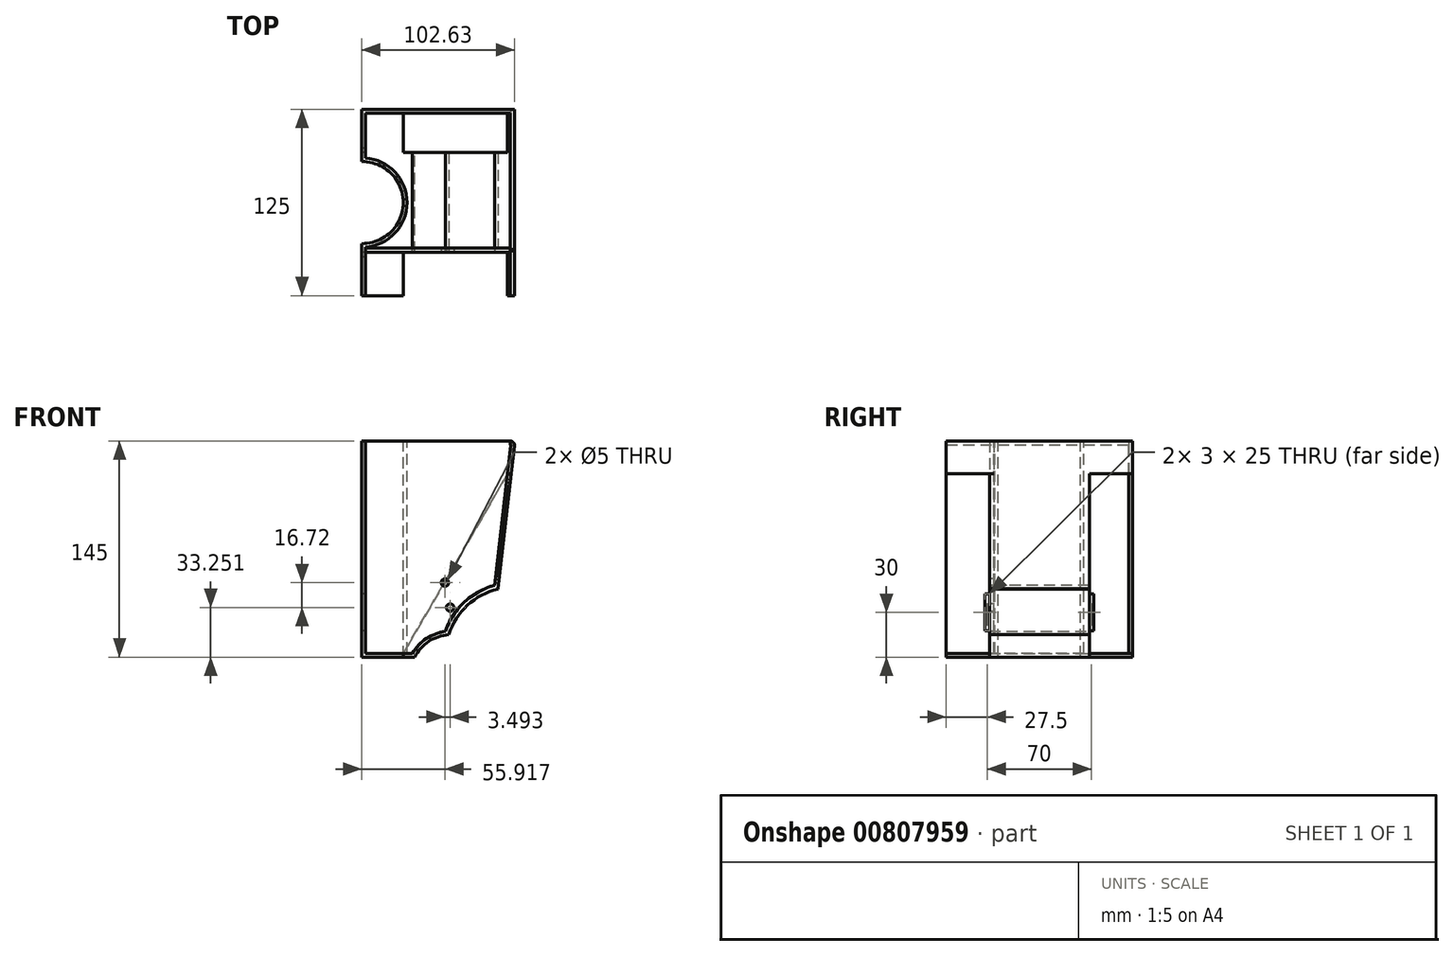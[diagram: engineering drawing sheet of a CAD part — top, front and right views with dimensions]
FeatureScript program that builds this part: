
annotation { "Feature Type Name" : "Feature", "Feature Type Description" : "" }
export const myFeature = defineFeature(function(context is Context, id is Id, definition is map)
    precondition{}
    {
        {
            var Q0;
            Q0=qCreatedBy(makeId("Front.planeOp"),FACE);
            var sketch = newSketch(context, id + "F0", { "sketchPlane" : qUnion([Q0])});
            skLineSegment(sketch, "E0", {"start": v(0, 130) * mm, "end": v(75, 130) * mm});
            skArc(sketch, "E1", {"start": v(56.58, -15) * mm, "mid": v(32.08, 0) * mm, "end": v(7.59, -15) * mm});
            skLineSegment(sketch, "E2", {"start": v(0, -15) * mm, "end": v(7.59, -15) * mm});
            skLineSegment(sketch, "E3.trimOffspring", {"start": v(56.58, -15) * mm, "end": v(58.27, -15) * mm});
            skLineSegment(sketch, "E4", {"start": v(75, 130) * mm, "end": v(58.27, -15) * mm});
            skLineSegment(sketch, "E5", {"start": v(0, 130) * mm, "end": v(-28, 130) * mm});
            skLineSegment(sketch, "E6", {"start": v(0, -15) * mm, "end": v(-28, -15) * mm});
            skLineSegment(sketch, "E7", {"start": v(-28, -15) * mm, "end": v(-28, 130) * mm});
            skLineSegment(sketch, "E8", {"start": v(75.45, 0) * mm, "end": v(-49.86, 0) * mm, "construction": true});
            skLineSegment(sketch, "E9", {"start": v(0, -37.66) * mm, "end": v(0, 158.2) * mm, "construction": true});
            skSolve(sketch);
        }
        {
            var Q0;
            Q0=makeQuery(id+"F0.imprint","IMPRINT",FACE,{"disambiguationData":[TD([[makeQuery(id+"F0.imprint","IMPRINT",EDGE,{"derivedFrom":sQuery(id+"F0.wireOp",EDGE,"AEWyvxpA-VYwD-7hNY-brtb-rKHveOHAXlaS")}),-1.0]])]});
            var Q1;
            Q1=makeQuery(id+"F0.imprint","IMPRINT",FACE,{"disambiguationData":[TD([[makeQuery(id+"F0.imprint","IMPRINT",EDGE,{"derivedFrom":sQuery(id+"F0.wireOp",EDGE,"E0")}),-1.0]])]});
            extrude(context, id + "F1", {"entities" : qUnion([Q0, Q1]), "depth" : 125 * mm, "offsetDistance" : 25 * mm});
        }
        {
            var Q0;
            Q0=makeQuery(id+"F1.opExtrude","SWEPT_FACE",FACE,{"disambiguationData":[OSD([sQuery(id+"F0.wireOp",EDGE,"E0"),sQuery(id+"F0.wireOp",EDGE,"E5")])]});
            cPlane(context, id + "F2", {"entities" : qUnion([Q0]), "cplaneType" : CPlaneType.OFFSET, "offset" : 0 * mm, "width" : 150 * mm, "height" : 150 * mm});
        }
        {
            var Q0;
            Q0=qCreatedBy(id+"F2.planeOp",FACE);
            var sketch = newSketch(context, id + "F3", { "sketchPlane" : qUnion([Q0])});
            skCircle(sketch, "E10", {"center": v(-27.5, -62.5) * mm, "radius": 27.5 * mm});
            skLineSegment(sketch, "E11", {"start": v(0, 0) * mm, "end": v(0, -125) * mm, "construction": true});
            skLineSegment(sketch, "E12", {"start": v(0, 0) * mm, "end": v(0, -62.5) * mm, "construction": true});
            skSolve(sketch);
        }
        {
            var Q0;
            Q0=makeQuery(id+"F3.imprint","IMPRINT",FACE,{"disambiguationData":[TD([[makeQuery(id+"F3.imprint","IMPRINT",EDGE,{"derivedFrom":sQuery(id+"F3.wireOp",EDGE,"E10")}),1.0]])]});
            extrude(context, id + "F4", {"entities" : qUnion([Q0]), "operationType" : NewBodyOperationType.REMOVE, "oppositeDirection" : true, "depth" : 171.8 * mm, "offsetDistance" : 25 * mm});
        }
        {
            var Q0;
            Q0=makeQuery(id+"F1.opExtrude","SWEPT_EDGE",EDGE,{"disambiguationData":[OSD([sQuery(id+"F0.wireOp",EDGE,"E0"),sQuery(id+"F0.wireOp",EDGE,"E4")])]});
            fillet(context, id + "F5", {"entities" : qUnion([Q0]), "radius" : 3 * mm, "tangentPropagation" : true, "allowEdgeOverflow" : false});
        }
        {
            var Q0;
            Q0=makeQuery(id+"F1.opExtrude","SWEPT_FACE",FACE,{"disambiguationData":[OSD([sQuery(id+"F0.wireOp",EDGE,"E0"),sQuery(id+"F0.wireOp",EDGE,"E5")])]});
            var Q1;
            Q1=makeQuery(id+"F1.opExtrude","CAP_FACE",FACE,{"disambiguationData":[OSD([sQuery(id+"F0.wireOp",EDGE,"E0"),sQuery(id+"F0.wireOp",EDGE,"E1"),sQuery(id+"F0.wireOp",EDGE,"E2"),sQuery(id+"F0.wireOp",EDGE,"E3.trimOffspring"),sQuery(id+"F0.wireOp",EDGE,"E4"),sQuery(id+"F0.wireOp",EDGE,"E5"),sQuery(id+"F0.wireOp",EDGE,"E6"),sQuery(id+"F0.wireOp",EDGE,"E7")])],"isStart":false});
            shell(context, id + "F6", {"entities" : qUnion([Q0, Q1]), "thickness" : 2.5 * mm});
        }
        {
            var Q0;
            {var subQ0=sQuery(id+"F0.wireOp",EDGE,"E7");var subQ1=sQuery(id+"F0.wireOp",EDGE,"E6");var subQ2=sQuery(id+"F0.wireOp",EDGE,"E5");var subQ3=sQuery(id+"F0.wireOp",EDGE,"E2");var subQ4=sQuery(id+"F0.wireOp",EDGE,"E0");Q0=makeQuery(id+"F4.boolean.opBoolean","SPLIT",FACE,{"disambiguationData":[TD([makeQuery(id+"F1.opExtrude","CAP_FACE",FACE,{"disambiguationData":[OSD([subQ4,sQuery(id+"F0.wireOp",EDGE,"E1"),subQ3,sQuery(id+"F0.wireOp",EDGE,"E3.trimOffspring"),sQuery(id+"F0.wireOp",EDGE,"E4"),subQ2,subQ1,subQ0])],"isStart":true})])],"derivedFrom":makeQuery(id+"F1.opExtrude","SWEPT_FACE",FACE,{"disambiguationData":[OSD([subQ0])]})});}
            cPlane(context, id + "F7", {"entities" : qUnion([Q0]), "cplaneType" : CPlaneType.OFFSET, "offset" : 0 * mm, "width" : 150 * mm, "height" : 150 * mm});
        }
        {
            var Q0;
            Q0=qCreatedBy(id+"F7.planeOp",FACE);
            var sketch = newSketch(context, id + "F8", { "sketchPlane" : qUnion([Q0])});
            skLineSegment(sketch, "E13.bottom", {"start": v(29, 2.5) * mm, "end": v(26, 2.5) * mm});
            skLineSegment(sketch, "E13.top", {"start": v(29, 27.5) * mm, "end": v(26, 27.5) * mm});
            skLineSegment(sketch, "E13.left", {"start": v(29, 2.5) * mm, "end": v(29, 27.5) * mm});
            skLineSegment(sketch, "E13.right", {"start": v(26, 2.5) * mm, "end": v(26, 27.5) * mm});
            skLineSegment(sketch, "E14.bottom", {"start": v(96, 2.5) * mm, "end": v(99, 2.5) * mm});
            skLineSegment(sketch, "E14.top", {"start": v(96, 27.5) * mm, "end": v(99, 27.5) * mm});
            skLineSegment(sketch, "E14.left", {"start": v(96, 2.5) * mm, "end": v(96, 27.5) * mm});
            skLineSegment(sketch, "E14.right", {"start": v(99, 2.5) * mm, "end": v(99, 27.5) * mm});
            skLineSegment(sketch, "E15.bottom", {"start": v(99, 2.5) * mm, "end": v(96, 2.5) * mm});
            skSolve(sketch);
        }
        {
            var Q0;
            Q0=makeQuery(id+"F8.imprint","IMPRINT",FACE,{"disambiguationData":[TD([[makeQuery(id+"F8.imprint","IMPRINT",EDGE,{"derivedFrom":sQuery(id+"F8.wireOp",EDGE,"E13.bottom")}),-1.0]])]});
            var Q1;
            Q1=makeQuery(id+"F8.imprint","IMPRINT",FACE,{"disambiguationData":[TD([[makeQuery(id+"F8.imprint","IMPRINT",EDGE,{"derivedFrom":sQuery(id+"F8.wireOp",EDGE,"E14.top")}),-1.0]])]});
            extrude(context, id + "F9", {"entities" : qUnion([Q0, Q1]), "operationType" : NewBodyOperationType.REMOVE, "oppositeDirection" : true, "depth" : 35.1 * mm, "offsetDistance" : 25 * mm});
        }
        {
            var Q0;
            Q0=qCreatedBy(id+"F7.planeOp",FACE);
            cPlane(context, id + "F10", {"entities" : qUnion([Q0]), "cplaneType" : CPlaneType.OFFSET, "offset" : 110 * mm, "oppositeDirection" : true, "width" : 150 * mm, "height" : 150 * mm});
        }
        {
            var Q0;
            Q0=qCreatedBy(id+"F10.planeOp",FACE);
            var sketch = newSketch(context, id + "F11", { "sketchPlane" : qUnion([Q0])});
            skLineSegment(sketch, "E16.bottom", {"start": v(102, -15) * mm, "end": v(99, -15) * mm});
            skLineSegment(sketch, "E16.top", {"start": v(102, 108) * mm, "end": v(99, 108) * mm});
            skLineSegment(sketch, "E16.left", {"start": v(102, -15) * mm, "end": v(102, 108) * mm});
            skLineSegment(sketch, "E16.right", {"start": v(99, -15) * mm, "end": v(99, 108) * mm});
            skLineSegment(sketch, "E17.bottom", {"start": v(26, -15) * mm, "end": v(23, -15) * mm});
            skLineSegment(sketch, "E17.top", {"start": v(26, 108) * mm, "end": v(23, 108) * mm});
            skLineSegment(sketch, "E17.left", {"start": v(26, -15) * mm, "end": v(26, 108) * mm});
            skLineSegment(sketch, "E17.right", {"start": v(23, -15) * mm, "end": v(23, 108) * mm});
            skSolve(sketch);
        }
        {
            var Q0;
            Q0=makeQuery(id+"F11.imprint","IMPRINT",FACE,{"disambiguationData":[TD([[makeQuery(id+"F11.imprint","IMPRINT",EDGE,{"derivedFrom":sQuery(id+"F11.wireOp",EDGE,"E16.bottom")}),-1.0]])]});
            var Q1;
            Q1=makeQuery(id+"F11.imprint","IMPRINT",FACE,{"disambiguationData":[TD([[makeQuery(id+"F11.imprint","IMPRINT",EDGE,{"derivedFrom":sQuery(id+"F11.wireOp",EDGE,"E17.bottom")}),-1.0]])]});
            extrude(context, id + "F12", {"entities" : qUnion([Q0, Q1]), "operationType" : NewBodyOperationType.REMOVE, "depth" : 23.73 * mm, "offsetDistance" : 25 * mm});
        }
        {
            var Q0;
            Q0=makeQuery(id+"F1.opExtrude","SWEPT_FACE",FACE,{"disambiguationData":[OSD([sQuery(id+"F0.wireOp",EDGE,"E2"),sQuery(id+"F0.wireOp",EDGE,"E6")])]});
            cPlane(context, id + "F13", {"entities" : qUnion([Q0]), "cplaneType" : CPlaneType.OFFSET, "offset" : 0 * mm, "width" : 150 * mm, "height" : 150 * mm});
        }
        {
            var Q0;
            Q0=makeQuery(id+"F1.opExtrude","CAP_FACE",FACE,{"disambiguationData":[OSD([sQuery(id+"F0.wireOp",EDGE,"E0"),sQuery(id+"F0.wireOp",EDGE,"E1"),sQuery(id+"F0.wireOp",EDGE,"E2"),sQuery(id+"F0.wireOp",EDGE,"E3.trimOffspring"),sQuery(id+"F0.wireOp",EDGE,"E4"),sQuery(id+"F0.wireOp",EDGE,"E5"),sQuery(id+"F0.wireOp",EDGE,"E6"),sQuery(id+"F0.wireOp",EDGE,"E7")])],"isStart":false});
            cPlane(context, id + "F14", {"entities" : qUnion([Q0]), "cplaneType" : CPlaneType.OFFSET, "offset" : 29 * mm, "oppositeDirection" : true, "width" : 150 * mm, "height" : 150 * mm});
        }
        {
            var Q0;
            Q0=qCreatedBy(id+"F14.planeOp",FACE);
            var sketch = newSketch(context, id + "F15", { "sketchPlane" : qUnion([Q0])});
            skCircle(sketch, "E18", {"center": v(73.93, -13.54) * mm, "radius": 45.5 * mm});
            skSolve(sketch);
        }
        {
            var Q0;
            Q0=makeQuery(id+"F15.imprint","IMPRINT",FACE,{"disambiguationData":[TD([[makeQuery(id+"F15.imprint","IMPRINT",EDGE,{"derivedFrom":sQuery(id+"F15.wireOp",EDGE,"E18")}),1.0]])]});
            var Q1;
            Q1=sQuery(id+"F15.wireOp",EDGE,"E18");
            extrude(context, id + "F16", {"entities" : qUnion([Q0]), "operationType" : NewBodyOperationType.REMOVE, "surfaceEntities" : qUnion([Q1]), "oppositeDirection" : true, "depth" : 70 * mm, "offsetDistance" : 25 * mm});
        }
        {
            var Q0;
            Q0=qCreatedBy(id+"F14.planeOp",FACE);
            var sketch = newSketch(context, id + "F17", { "sketchPlane" : qUnion([Q0])});
            skArc(sketch, "E19", {"start": v(63.52, 30.66) * mm, "mid": v(43, 19.72) * mm, "end": v(30.56, 0.06) * mm});
            skArc(sketch, "E20", {"start": v(63.89, 33.82) * mm, "mid": v(40.86, 21.83) * mm, "end": v(27.32, -0.31) * mm});
            skArc(sketch, "E21", {"start": v(30.56, 0.06) * mm, "mid": v(28.93, -0.08) * mm, "end": v(27.32, -0.31) * mm});
            skLineSegment(sketch, "E22", {"start": v(63.52, 30.66) * mm, "end": v(63.89, 33.82) * mm});
            skLineSegment(sketch, "E23", {"start": v(63.89, 33.82) * mm, "end": v(63.52, 30.66) * mm});
            skSolve(sketch);
        }
        {
            var Q0;
            Q0 = qSketchRegion(id + "F17", true);
            extrude(context, id + "F18", {"entities" : qUnion([Q0]), "oppositeDirection" : true, "depth" : 70 * mm, "offsetDistance" : 25 * mm});
        }
        {
            var Q0;
            Q0=makeQuery(id+"F18.opExtrude","SWEPT_BODY",BODY,{"disambiguationData":[OSD([sQuery(id+"F17.wireOp",EDGE,"E19"),sQuery(id+"F17.wireOp",EDGE,"E20"),sQuery(id+"F17.wireOp",EDGE,"E21"),sQuery(id+"F17.wireOp",EDGE,"E23")])]});
            var Q1;
            Q1=makeQuery(id+"F1.opExtrude","SWEPT_BODY",BODY,{"disambiguationData":[OSD([sQuery(id+"F0.wireOp",EDGE,"E0"),sQuery(id+"F0.wireOp",EDGE,"E1"),sQuery(id+"F0.wireOp",EDGE,"E2"),sQuery(id+"F0.wireOp",EDGE,"E3.trimOffspring"),sQuery(id+"F0.wireOp",EDGE,"E4"),sQuery(id+"F0.wireOp",EDGE,"E5"),sQuery(id+"F0.wireOp",EDGE,"E6"),sQuery(id+"F0.wireOp",EDGE,"E7")])]});
            booleanBodies(context, id + "F19", {"operationType" : BooleanOperationType.UNION, "tools" : qUnion([Q0, Q1])});
        }
        {
            var Q0;
            Q0=qCreatedBy(id+"F14.planeOp",FACE);
            var sketch = newSketch(context, id + "F20", { "sketchPlane" : qUnion([Q0])});
            skLineSegment(sketch, "E24", {"start": v(0, -12.59) * mm, "end": v(0, -15.04) * mm});
            skLineSegment(sketch, "E25", {"start": v(0, -15.04) * mm, "end": v(58.34, -15.04) * mm});
            skLineSegment(sketch, "E26", {"start": v(58.34, -15.04) * mm, "end": v(72.46, 108) * mm});
            skLineSegment(sketch, "E27", {"start": v(69.95, 108) * mm, "end": v(0, -12.59) * mm});
            skLineSegment(sketch, "E28", {"start": v(69.95, 108) * mm, "end": v(72.46, 108) * mm});
            skSolve(sketch);
        }
        {
            var Q0;
            Q0=makeQuery(id+"F20.imprint","IMPRINT",FACE,{"disambiguationData":[TD([[makeQuery(id+"F20.imprint","IMPRINT",EDGE,{"derivedFrom":sQuery(id+"F20.wireOp",EDGE,"E24")}),1.0]])]});
            extrude(context, id + "F21", {"entities" : qUnion([Q0]), "operationType" : NewBodyOperationType.REMOVE, "depth" : 47.2 * mm, "offsetDistance" : 25 * mm});
        }
        {
            var Q0;
            Q0=makeQuery(id+"F1.opExtrude","CAP_FACE",FACE,{"disambiguationData":[OSD([sQuery(id+"F0.wireOp",EDGE,"E0"),sQuery(id+"F0.wireOp",EDGE,"E1"),sQuery(id+"F0.wireOp",EDGE,"E2"),sQuery(id+"F0.wireOp",EDGE,"E3.trimOffspring"),sQuery(id+"F0.wireOp",EDGE,"E4"),sQuery(id+"F0.wireOp",EDGE,"E5"),sQuery(id+"F0.wireOp",EDGE,"E6"),sQuery(id+"F0.wireOp",EDGE,"E7")])],"isStart":true});
            var sketch = newSketch(context, id + "F22", { "sketchPlane" : qUnion([Q0])});
            skLineSegment(sketch, "E29", {"start": v(-72.46, 108.01) * mm, "end": v(-69.95, 108.01) * mm});
            skLineSegment(sketch, "E30", {"start": v(-69.95, 108.01) * mm, "end": v(0, -12.5) * mm});
            skLineSegment(sketch, "E31", {"start": v(0, -12.5) * mm, "end": v(0, -15) * mm});
            skLineSegment(sketch, "E32", {"start": v(0, -15) * mm, "end": v(-58.27, -15) * mm});
            skLineSegment(sketch, "E33", {"start": v(-58.27, -15) * mm, "end": v(-72.46, 108.01) * mm});
            skSolve(sketch);
        }
        {
            var Q0;
            Q0=makeQuery(id+"F22.imprint","IMPRINT",FACE,{"disambiguationData":[TD([[makeQuery(id+"F22.imprint","IMPRINT",EDGE,{"derivedFrom":sQuery(id+"F22.wireOp",EDGE,"E29")}),-1.0]])]});
            extrude(context, id + "F23", {"entities" : qUnion([Q0]), "operationType" : NewBodyOperationType.REMOVE, "oppositeDirection" : true, "depth" : 29 * mm, "offsetDistance" : 25 * mm});
        }
        {
            var Q0;
            Q0=qCreatedBy(id+"F14.planeOp",FACE);
            var sketch = newSketch(context, id + "F24", { "sketchPlane" : qUnion([Q0])});
            skLineSegment(sketch, "E34", {"start": v(-25.38, 129.9) * mm, "end": v(72.56, 129.9) * mm});
            skLineSegment(sketch, "E35", {"start": v(72.56, 129.9) * mm, "end": v(72.46, 108) * mm});
            skLineSegment(sketch, "E36", {"start": v(72.46, 108) * mm, "end": v(61.31, 33.2) * mm});
            skLineSegment(sketch, "E37", {"start": v(6.1, -12.5) * mm, "end": v(-25.38, -12.5) * mm});
            skLineSegment(sketch, "E38", {"start": v(-25.38, -12.5) * mm, "end": v(-25.38, 129.9) * mm});
            skFitSpline(sketch, "E39", {"points": [v(6.1, -12.5) * mm, v(28.12, 2.24) * mm], "startDerivative": vector(19.49, 27.96) * mm, "endDerivative": vector(30.75, 6.71) * mm});
            skFitSpline(sketch, "E40", {"points": [v(28.12, 2.24) * mm, v(61.31, 33.2) * mm], "startDerivative": vector(15.06, 41.23) * mm, "endDerivative": vector(53.08, 14.78) * mm});
            skCircle(sketch, "E41", {"center": v(27.92, 34.97) * mm, "radius": 2.5 * mm});
            skCircle(sketch, "E42", {"center": v(31.4, 18.25) * mm, "radius": 2.5 * mm});
            skSolve(sketch);
        }
        {
            var Q0;
            Q0=makeQuery(id+"F24.imprint","IMPRINT",FACE,{"disambiguationData":[TD([[makeQuery(id+"F24.imprint","IMPRINT",EDGE,{"derivedFrom":sQuery(id+"F24.wireOp",EDGE,"E34")}),-1.0]])]});
            extrude(context, id + "F25", {"entities" : qUnion([Q0]), "oppositeDirection" : true, "depth" : 3 * mm, "offsetDistance" : 25 * mm});
        }
    });
